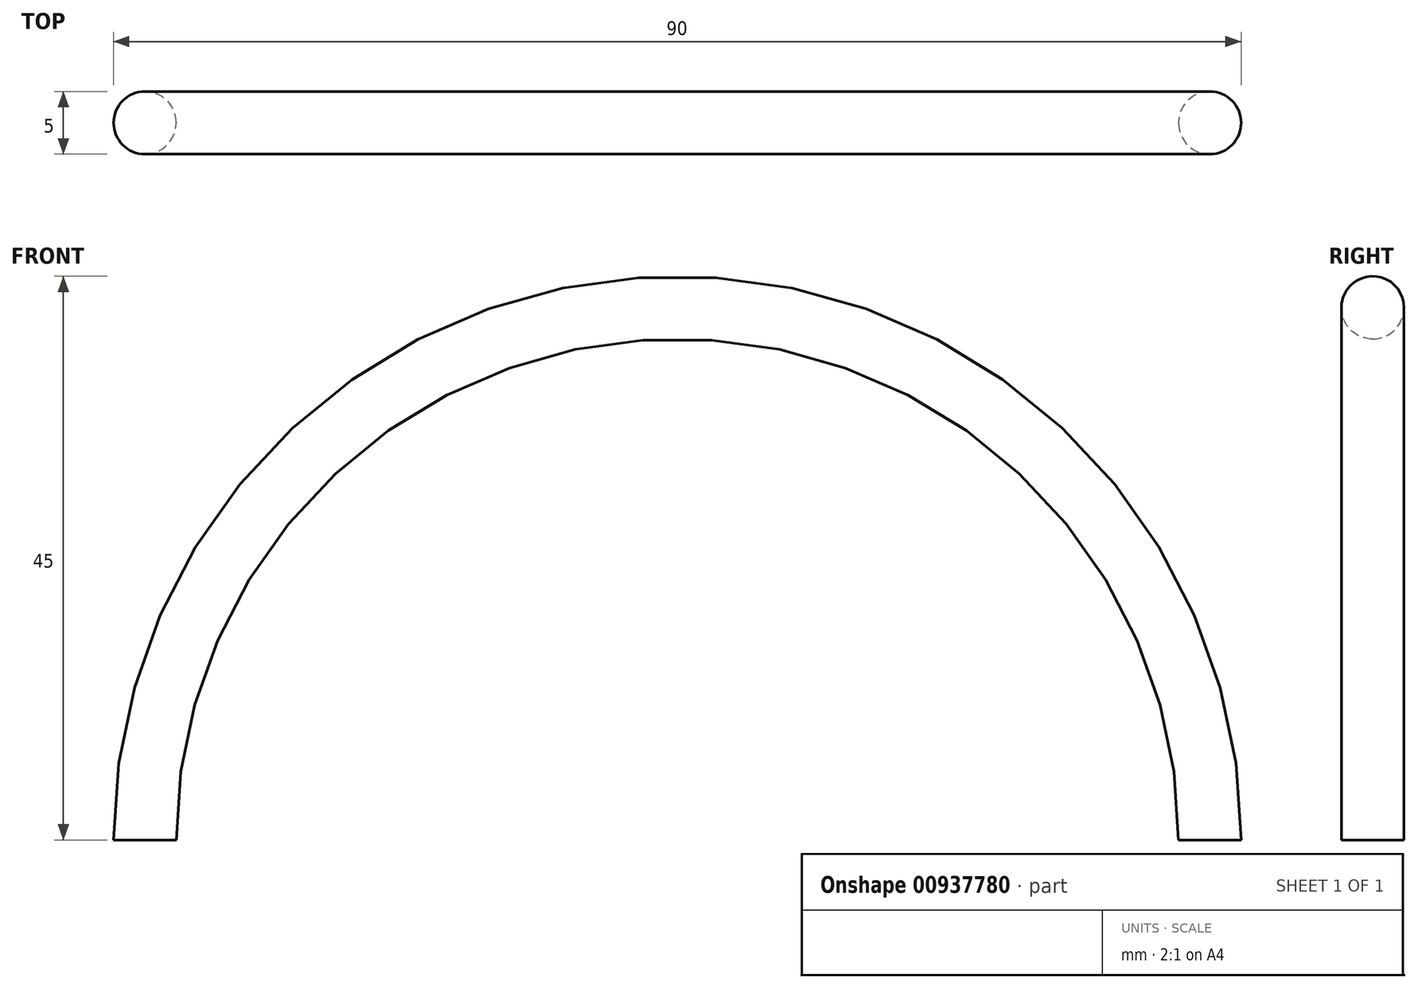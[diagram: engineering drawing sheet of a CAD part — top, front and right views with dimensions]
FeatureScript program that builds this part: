
annotation { "Feature Type Name" : "Feature", "Feature Type Description" : "" }
export const myFeature = defineFeature(function(context is Context, id is Id, definition is map)
    precondition{}
    {
        {
            var Q0;
            Q0=qCreatedBy(makeId("Front.planeOp"),FACE);
            var sketch = newSketch(context, id + "F0", { "sketchPlane" : qUnion([Q0])});
            skArc(sketch, "E0", {"start": v(42.5, 0) * mm, "mid": v(0, 42.5) * mm, "end": v(-42.5, 0) * mm});
            skPoint(sketch, "E1", {"position": v(-42.5, 0) * mm});
            skPoint(sketch, "E2", {"position": v(31.14, -28.92) * mm});
            skLineSegment(sketch, "E3", {"start": v(0, 0) * mm, "end": v(42.5, 0) * mm});
            skSolve(sketch);
        }
        {
            var Q0;
            Q0=qCreatedBy(makeId("Top.planeOp"),FACE);
            var sketch = newSketch(context, id + "F1", { "sketchPlane" : qUnion([Q0])});
            skCircle(sketch, "E4", {"center": v(-42.5, 0) * mm, "radius": 2.5 * mm});
            skSolve(sketch);
        }
        {
            var Q0;
            Q0=makeQuery(id+"F1.imprint","IMPRINT",FACE,{"disambiguationData":[TD([[makeQuery(id+"F1.imprint","IMPRINT",EDGE,{"derivedFrom":sQuery(id+"F1.wireOp",EDGE,"E4")}),1.0]])]});
            var Q1;
            Q1=sQuery(id+"F0.wireOp",EDGE,"E0");
            sweep(context, id + "F2", {"profiles" : qUnion([Q0]), "path" : qUnion([Q1])});
        }
    });
